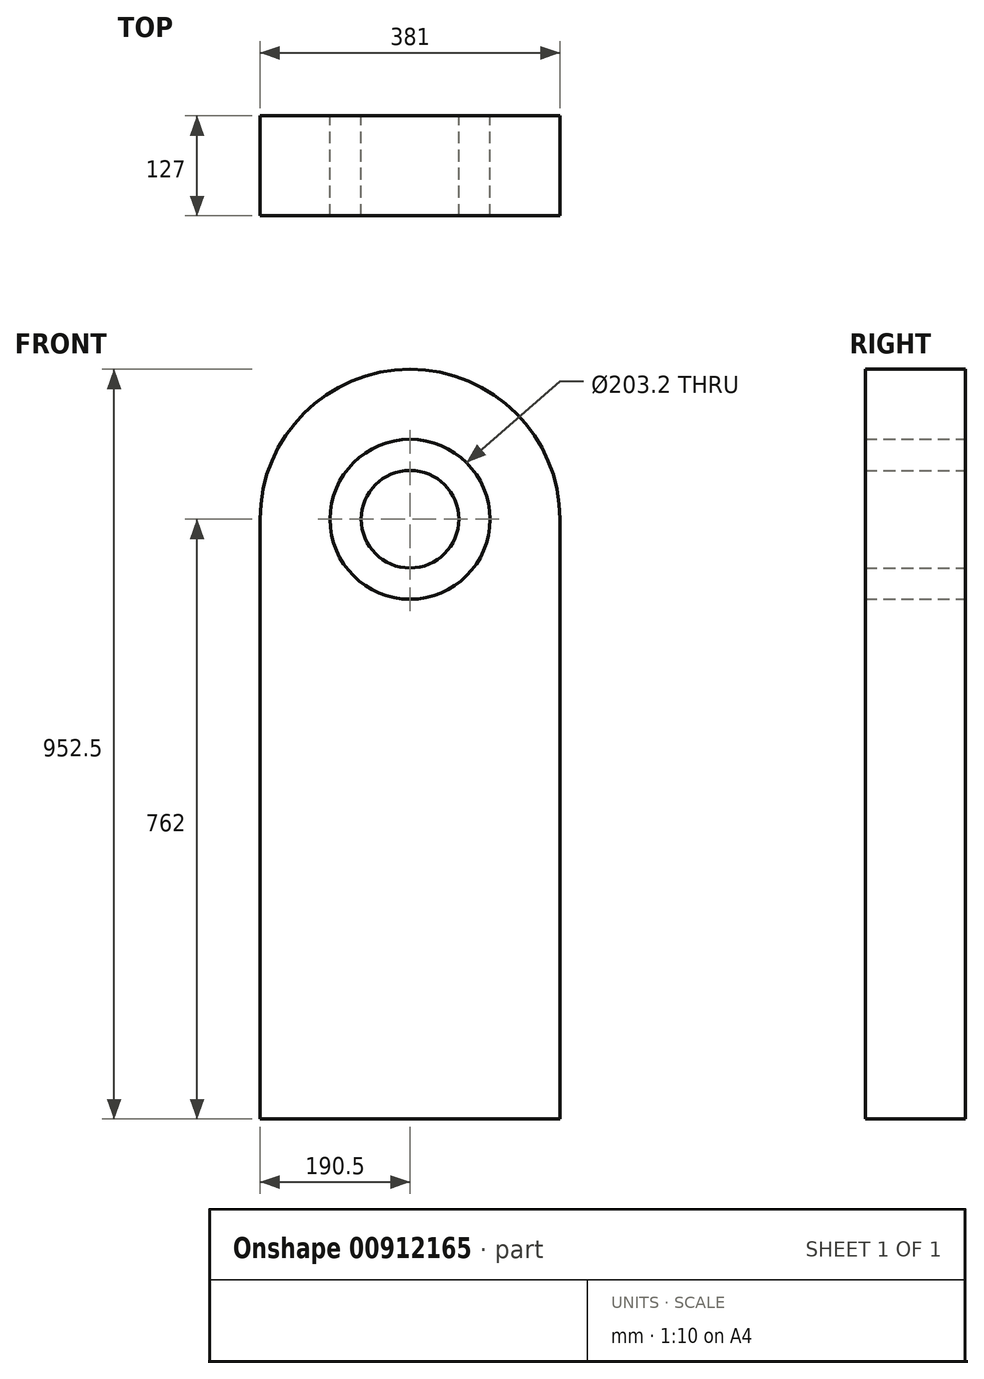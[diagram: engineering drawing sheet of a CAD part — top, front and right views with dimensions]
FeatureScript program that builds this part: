
annotation { "Feature Type Name" : "Feature", "Feature Type Description" : "" }
export const myFeature = defineFeature(function(context is Context, id is Id, definition is map)
    precondition{}
    {
        {
            var Q0;
            Q0=qCreatedBy(makeId("Front.planeOp"),FACE);
            var sketch = newSketch(context, id + "F0", { "sketchPlane" : qUnion([Q0])});
            skLineSegment(sketch, "E0.bottom", {"start": v(-190.5, 0) * mm, "end": v(190.5, 0) * mm});
            skLineSegment(sketch, "E0.left", {"start": v(-190.5, 0) * mm, "end": v(-190.5, 762) * mm});
            skLineSegment(sketch, "E0.right", {"start": v(190.5, 0) * mm, "end": v(190.5, 762) * mm});
            skArc(sketch, "E1", {"start": v(190.5, 762) * mm, "mid": v(0, 952.5) * mm, "end": v(-190.5, 762) * mm});
            skCircle(sketch, "E2", {"center": v(0, 762) * mm, "radius": 101.6 * mm});
            skCircle(sketch, "E3", {"center": v(0, 762) * mm, "radius": 61.98 * mm});
            skSolve(sketch);
        }
        {
            var Q0;
            Q0 = qSketchRegion(id + "F0", true);
            var Q1;
            Q1=makeQuery(id+"F0.imprint","IMPRINT",FACE,{"disambiguationData":[TD([[makeQuery(id+"F0.imprint","IMPRINT",EDGE,{"derivedFrom":sQuery(id+"F0.wireOp",EDGE,"E3")}),1.0]])]});
            extrude(context, id + "F1", {"entities" : qUnion([Q0, Q1]), "depth" : 127 * mm, "offsetDistance" : 25.4 * mm});
        }
    });
